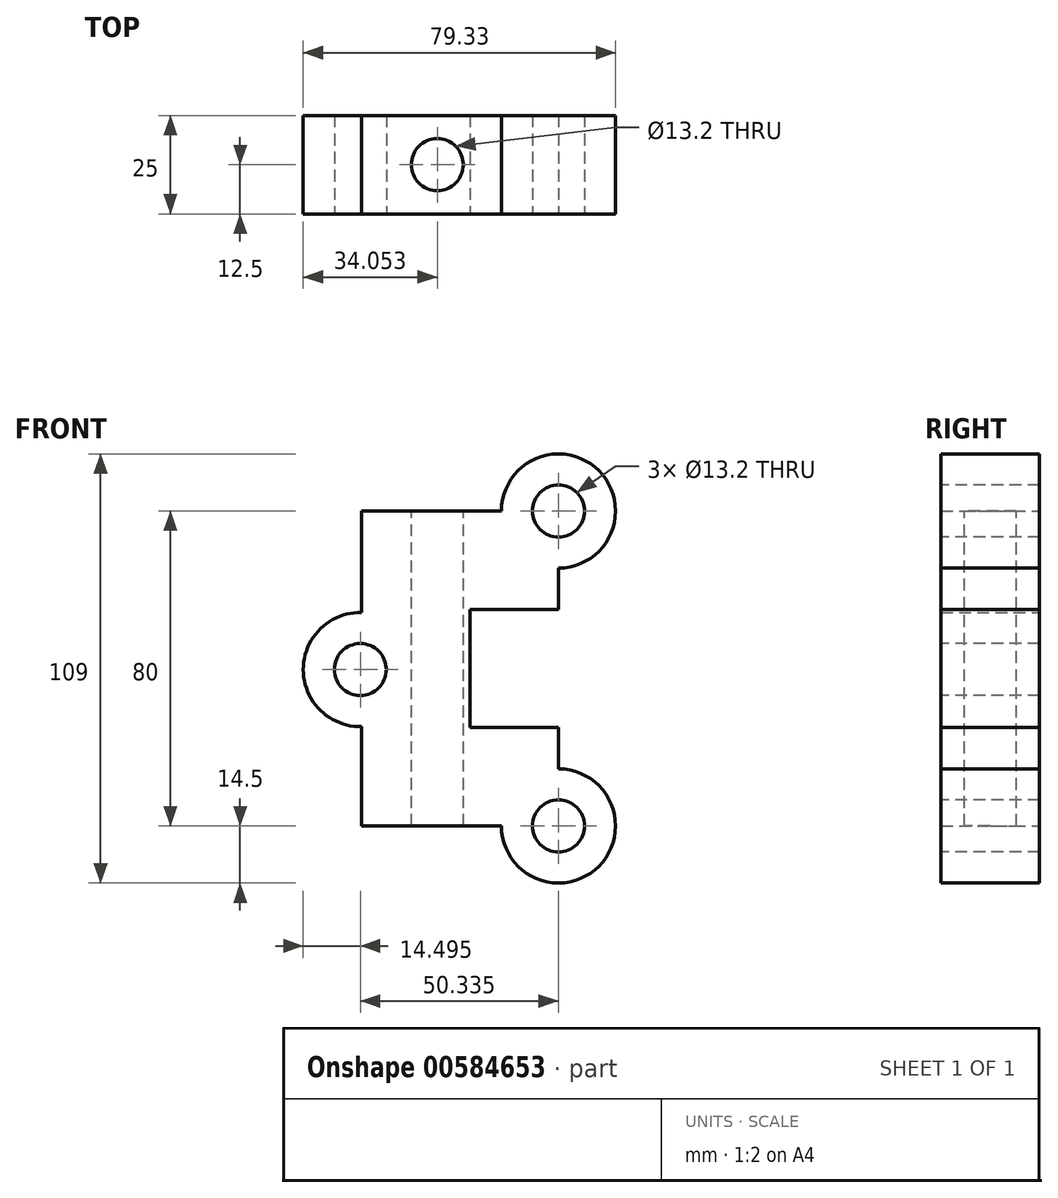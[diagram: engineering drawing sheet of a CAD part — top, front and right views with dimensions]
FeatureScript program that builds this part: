
annotation { "Feature Type Name" : "Feature", "Feature Type Description" : "" }
export const myFeature = defineFeature(function(context is Context, id is Id, definition is map)
    precondition{}
    {
        {
            var Q0;
            Q0=qCreatedBy(makeId("Front.planeOp"),FACE);
            var sketch = newSketch(context, id + "F0", { "sketchPlane" : qUnion([Q0])});
            skLineSegment(sketch, "E0.bottom", {"start": v(25, -40) * mm, "end": v(-25, -40) * mm});
            skLineSegment(sketch, "E0.top", {"start": v(25, 40) * mm, "end": v(-25, 40) * mm});
            skLineSegment(sketch, "E0.left", {"start": v(25, -40) * mm, "end": v(25, 40) * mm});
            skLineSegment(sketch, "E0.right", {"start": v(-25, -40) * mm, "end": v(-25, 40) * mm});
            skPoint(sketch, "E0.middle", {"position": v(0, 0) * mm});
            skCircle(sketch, "E1", {"center": v(25, 40) * mm, "radius": 14.5 * mm});
            skCircle(sketch, "E2", {"center": v(25, -40) * mm, "radius": 14.5 * mm});
            skCircle(sketch, "E3", {"center": v(-25.33, -0.28) * mm, "radius": 14.5 * mm});
            skSolve(sketch);
        }
        {
            var Q0;
            Q0=qSketchRegion(id+"F0",true);
            extrude(context, id + "F1", {"entities" : qUnion([Q0]), "endBound" : BoundingType.SYMMETRIC, "depth" : 25 * mm, "offsetDistance" : 25 * mm});
        }
        {
            var Q0;
            Q0=makeQuery(id+"F1.opExtrude","CAP_FACE",FACE,{"disambiguationData":[OSD([sQuery(id+"F0.wireOp",EDGE,"E0.bottom"),sQuery(id+"F0.wireOp",EDGE,"E0.top"),sQuery(id+"F0.wireOp",EDGE,"E0.left"),sQuery(id+"F0.wireOp",EDGE,"E0.right"),sQuery(id+"F0.wireOp",EDGE,"E1"),sQuery(id+"F0.wireOp",EDGE,"E2"),sQuery(id+"F0.wireOp",EDGE,"E3")])],"isStart":false});
            var sketch = newSketch(context, id + "F2", { "sketchPlane" : qUnion([Q0])});
            skPoint(sketch, "E4", {"position": v(25, 40) * mm});
            skPoint(sketch, "E5", {"position": v(25, -40) * mm});
            skPoint(sketch, "E6", {"position": v(-25.33, -0.28) * mm});
            skSolve(sketch);
        }
        {
            var Q0;
            Q0=sQuery(id+"F2.wireOp",VERTEX,"E4");
            var Q1;
            Q1=sQuery(id+"F2.wireOp",VERTEX,"E6");
            var Q2;
            Q2=sQuery(id+"F2.wireOp",VERTEX,"E5");
            var Q3;
            Q3=makeQuery(id+"F1.opExtrude","SWEPT_BODY",BODY,{"disambiguationData":[OSD([sQuery(id+"F0.wireOp",EDGE,"E0.bottom"),sQuery(id+"F0.wireOp",EDGE,"E0.top"),sQuery(id+"F0.wireOp",EDGE,"E0.left"),sQuery(id+"F0.wireOp",EDGE,"E0.right"),sQuery(id+"F0.wireOp",EDGE,"E1"),sQuery(id+"F0.wireOp",EDGE,"E2"),sQuery(id+"F0.wireOp",EDGE,"E3")])]});
            hole(context, id + "F3", {"style" : HoleStyle.C_BORE, "endStyle" : HoleEndStyle.THROUGH, "holeDiameter" : 13.2 * mm, "cBoreDiameter" : 19.25 * mm, "cBoreDepth" : 0 * mm, "majorDiameter" : 5 * mm, "isTappedThrough" : true, "tappedDepth" : 12 * mm, "tapClearance" : 3, "startFromSketch" : true, "locations" : qUnion([Q0, Q1, Q2]), "scope" : qUnion([Q3])});
        }
        {
            var Q0;
            Q0=makeQuery(id+"F1.opExtrude","SWEPT_FACE",FACE,{"disambiguationData":[OSD([sQuery(id+"F0.wireOp",EDGE,"E0.top")])]});
            var sketch = newSketch(context, id + "F4", { "sketchPlane" : qUnion([Q0])});
            skPoint(sketch, "E7", {"position": v(-5.78, 0) * mm});
            skSolve(sketch);
        }
        {
            var Q0;
            Q0=sQuery(id+"F4.wireOp",VERTEX,"E7");
            var Q1;
            Q1=makeQuery(id+"F1.opExtrude","SWEPT_BODY",BODY,{"disambiguationData":[OSD([sQuery(id+"F0.wireOp",EDGE,"E0.bottom"),sQuery(id+"F0.wireOp",EDGE,"E0.top"),sQuery(id+"F0.wireOp",EDGE,"E0.left"),sQuery(id+"F0.wireOp",EDGE,"E0.right"),sQuery(id+"F0.wireOp",EDGE,"E1"),sQuery(id+"F0.wireOp",EDGE,"E2"),sQuery(id+"F0.wireOp",EDGE,"E3")])]});
            hole(context, id + "F5", {"style" : HoleStyle.C_BORE, "endStyle" : HoleEndStyle.THROUGH, "holeDiameter" : 13.2 * mm, "cBoreDiameter" : 19.25 * mm, "cBoreDepth" : 0 * mm, "majorDiameter" : 5 * mm, "isTappedThrough" : true, "tappedDepth" : 12 * mm, "tapClearance" : 3, "startFromSketch" : true, "locations" : qUnion([Q0]), "scope" : qUnion([Q1])});
        }
        {
            var Q0;
            Q0=makeQuery(id+"F1.opExtrude","CAP_FACE",FACE,{"disambiguationData":[OSD([sQuery(id+"F0.wireOp",EDGE,"E0.bottom"),sQuery(id+"F0.wireOp",EDGE,"E0.top"),sQuery(id+"F0.wireOp",EDGE,"E0.left"),sQuery(id+"F0.wireOp",EDGE,"E0.right"),sQuery(id+"F0.wireOp",EDGE,"E1"),sQuery(id+"F0.wireOp",EDGE,"E2"),sQuery(id+"F0.wireOp",EDGE,"E3")])],"isStart":false});
            var sketch = newSketch(context, id + "F6", { "sketchPlane" : qUnion([Q0])});
            skLineSegment(sketch, "E8.bottom", {"start": v(2.5, 15) * mm, "end": v(47.5, 15) * mm});
            skLineSegment(sketch, "E8.top", {"start": v(2.5, -15) * mm, "end": v(47.5, -15) * mm});
            skLineSegment(sketch, "E8.left", {"start": v(2.5, 15) * mm, "end": v(2.5, -15) * mm});
            skLineSegment(sketch, "E8.right", {"start": v(47.5, 15) * mm, "end": v(47.5, -15) * mm});
            skPoint(sketch, "E8.middle", {"position": v(25, 0) * mm});
            skSolve(sketch);
        }
        {
            var Q0;
            Q0 = qSketchRegion(id + "F6", true);
            extrude(context, id + "F7", {"entities" : qUnion([Q0]), "operationType" : NewBodyOperationType.REMOVE, "oppositeDirection" : true, "depth" : 30 * mm, "offsetDistance" : 25 * mm});
        }
    });
